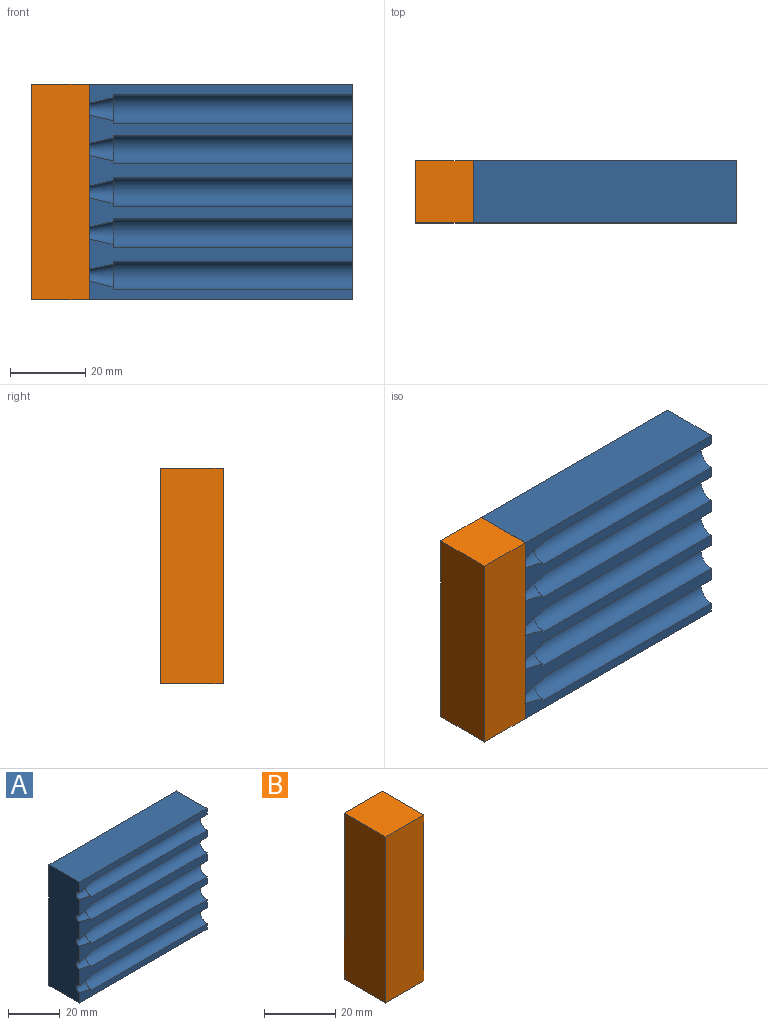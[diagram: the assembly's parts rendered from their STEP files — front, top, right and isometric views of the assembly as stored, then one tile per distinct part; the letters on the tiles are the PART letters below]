
ASSEMBLY  parts=2 mates=1
PART A: 30 faces, bbox 69.9x18x57.2 mm
  f0: plane 57.15x16.51mm, normal (-1,0,0), area 923.6mm2, adj f1,f2,f3,f4,f5,f7,f8,f10
  f1: plane 69.85x7.73mm, normal (0,-1,0), area 246.4mm2, adj f0,f6,f9,f12,f17,f18,f21,f28
  f2: plane 69.85x5.02mm, normal (0,-1,0), area 202.4mm2, adj f0,f7,f9,f15,f16,f26
  f3: plane 69.86x8mm, normal (0,-1,0), area 275mm2, adj f0,f9,f13,f14,f17,f18,f24,f29
  f4: plane 69.85x7.49mm, normal (0,-1,0), area 233.2mm2, adj f0,f9,f15,f16,f19,f20,f22,f27
  f5: plane 69.85x4.92mm, normal (0,-1,0), area 191.2mm2, adj f0,f8,f9,f13,f14,f25
  f6: plane 7.62x3.81mm, normal (1,0,0), area 8.2mm2, adj f1,f10,f12,f21
  f7: plane 69.85x16.51mm, normal (0,0,1), area 1153.2mm2, adj f0,f2,f9,f11
  f8: plane 69.85x16.51mm, normal (0,0,-1), area 1153.2mm2, adj f0,f5,f9,f11
  f9: plane 57.15x16.51mm, normal (1,0,0), area 829.5mm2, adj f1,f2,f3,f4,f5,f7,f8,f10
  f10: plane 69.85x8.11mm, normal (0,-1,0), area 276.9mm2, adj f0,f6,f9,f12,f19,f20,f21,f23
  f11: plane 69.85x57.15mm, normal (0,1,0), area 3991.9mm2, adj f0,f7,f8,f9
  f12: cylinder r=3.81mm len=63.5mm, axis (1,0,0), area 760.1mm2, adj f1,f6,f9,f10
  f13: cylinder r=3.81mm len=63.5mm, axis (1,0,0), area 760.1mm2, adj f3,f5,f9,f14
  f14: plane 7.62x3.81mm, normal (1,0,0), area 8.1mm2, adj f3,f5,f13,f24,f25
  f15: cylinder r=3.81mm len=63.5mm, axis (1,0,0), area 760.1mm2, adj f2,f4,f9,f16
  f16: plane 7.62x3.81mm, normal (1,0,0), area 8.1mm2, adj f2,f4,f15,f26,f27
  f17: cylinder r=3.81mm len=63.5mm, axis (1,0,0), area 760.1mm2, adj f1,f3,f9,f18
  f18: plane 7.62x3.81mm, normal (1,0,0), area 7.9mm2, adj f1,f3,f17,f28,f29
  f19: cylinder r=3.81mm len=63.5mm, axis (1,0,0), area 760.1mm2, adj f4,f9,f10,f20
  f20: plane 7.62x3.81mm, normal (1,0,0), area 8.1mm2, adj f4,f10,f19,f22,f23
  f21: cone r=3.05mm half-angle=12.9deg, axis (1,0,0), area 47.6mm2, adj f0,f1,f6,f10
  f22: bspline ~6.35x6.11mm, area 47.5mm2, adj f0,f4,f20,f23
  f23: bspline ~6.35x1.46mm, area 0mm2, adj f10,f20,f22
  f24: bspline ~6.35x1.86mm, area 0mm2, adj f3,f14,f25
  f25: bspline ~6.35x6.11mm, area 47.5mm2, adj f0,f5,f14,f24
  f26: bspline ~6.35x6.11mm, area 47.6mm2, adj f0,f2,f16,f27
  f27: bspline ~6.35x1.42mm, area 0.2mm2, adj f4,f16,f26
  f28: bspline ~6.35x1.5mm, area 0.5mm2, adj f1,f18,f29
  f29: bspline ~6.35x6.1mm, area 47.6mm2, adj f0,f3,f18,f28
PART B: 6 faces, bbox 15.2x16.5x57.2 mm
  f0: plane 57.15x16.51mm, normal (-1,0,0), area 943.5mm2, adj f1,f3,f4,f5
  f1: plane 16.51x15.24mm, normal (0,0,-1), area 251.6mm2, adj f0,f2,f4,f5
  f2: plane 57.15x16.51mm, normal (1,0,0), area 943.5mm2, adj f1,f3,f4,f5
  f3: plane 16.51x15.24mm, normal (0,0,1), area 251.6mm2, adj f0,f2,f4,f5
  f4: plane 57.15x15.24mm, normal (0,-1,0), area 871mm2, adj f0,f1,f2,f3
  f5: plane 57.15x15.24mm, normal (0,1,0), area 871mm2, adj f0,f1,f2,f3
PLACE A t=(9.45,-4.99,11.23)mm
PLACE B t=(-66.41,-4.95,18.29)mm
MATE planar B.f2 <-> A.f0  axis (1,0,0) through (-51.17,-13.2,46.87)mm
